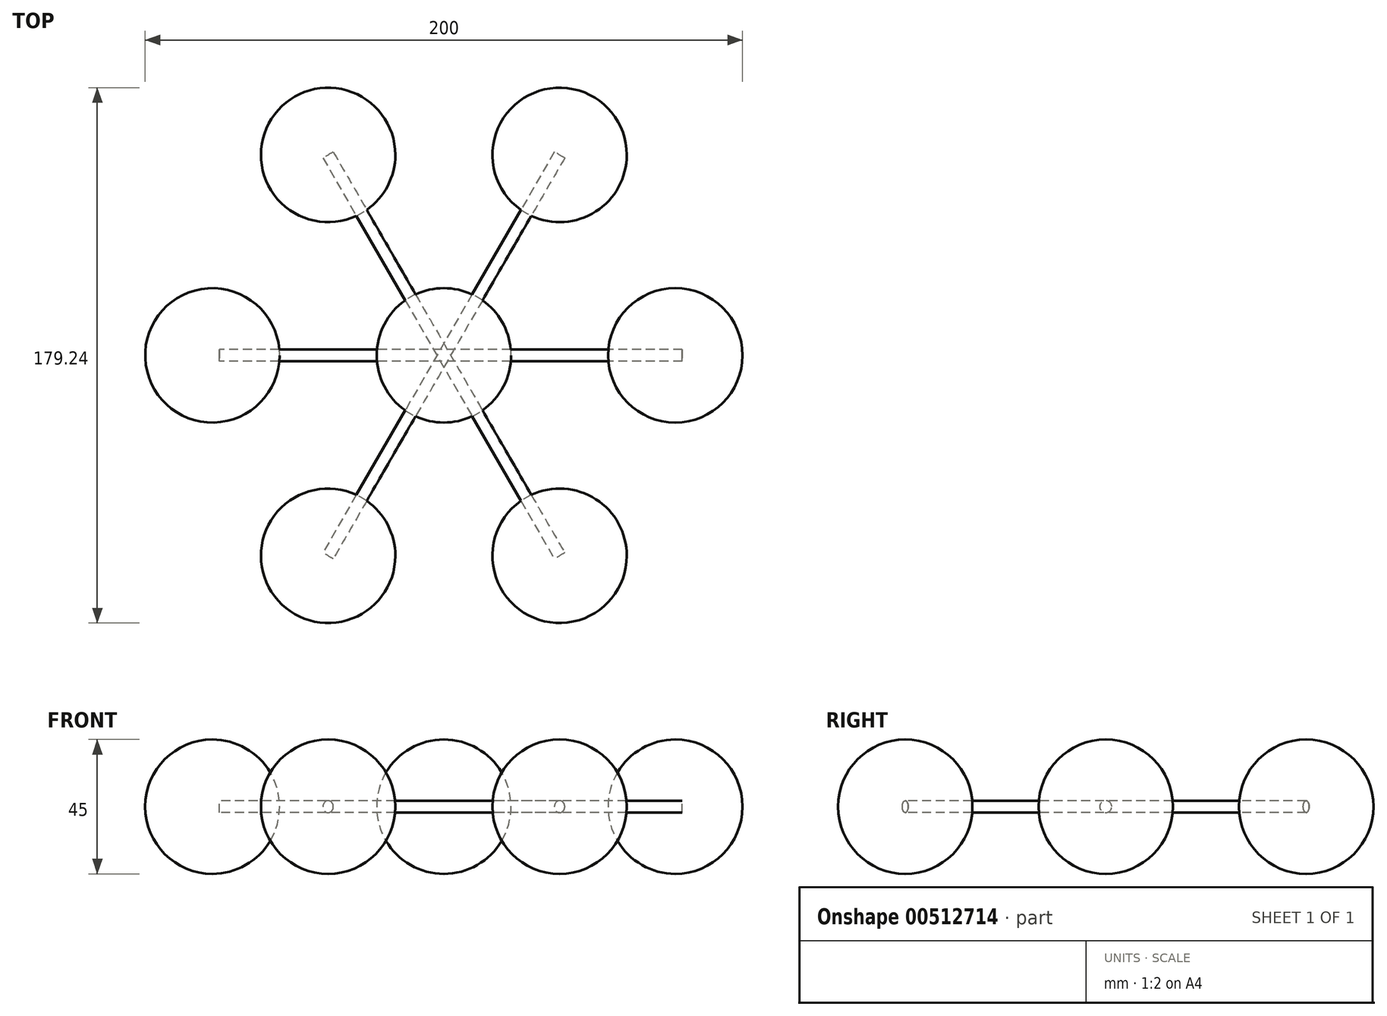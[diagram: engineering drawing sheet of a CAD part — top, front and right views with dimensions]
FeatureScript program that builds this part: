
annotation { "Feature Type Name" : "Feature", "Feature Type Description" : "" }
export const myFeature = defineFeature(function(context is Context, id is Id, definition is map)
    precondition{}
    {
        {
            var Q0;
            Q0=qCreatedBy(makeId("Top.planeOp"),FACE);
            var sketch = newSketch(context, id + "F0", { "sketchPlane" : qUnion([Q0])});
            skPoint(sketch, "E0.center", {"position": v(0, 0) * mm});
            skLineSegment(sketch, "E1", {"start": v(0, 75.54) * mm, "end": v(0, -76.03) * mm, "construction": true});
            skLineSegment(sketch, "E2", {"start": v(-100, 0) * mm, "end": v(100, 0) * mm, "construction": true});
            skLineSegment(sketch, "E3", {"start": v(100, 0) * mm, "end": v(55, 0) * mm});
            skCircle(sketch, "E4", {"center": v(0, 0) * mm, "radius": 22.5 * mm});
            skLineSegment(sketch, "E5", {"start": v(-50, 86.6) * mm, "end": v(0, 0) * mm, "construction": true});
            skLineSegment(sketch, "E6", {"start": v(0, 0) * mm, "end": v(50, 86.6) * mm, "construction": true});
            skLineSegment(sketch, "E7", {"start": v(0, 0) * mm, "end": v(-50, -86.6) * mm, "construction": true});
            skLineSegment(sketch, "E8", {"start": v(0, 0) * mm, "end": v(50, -86.6) * mm, "construction": true});
            skLineSegment(sketch, "E9", {"start": v(50, 86.6) * mm, "end": v(27.5, 47.63) * mm});
            skLineSegment(sketch, "E10", {"start": v(-50, 86.6) * mm, "end": v(-27.5, 47.63) * mm});
            skLineSegment(sketch, "E11", {"start": v(50, -86.6) * mm, "end": v(27.5, -47.63) * mm});
            skLineSegment(sketch, "E12", {"start": v(-50, -86.6) * mm, "end": v(-27.5, -47.63) * mm});
            skCircle(sketch, "E13", {"center": v(-38.75, 67.12) * mm, "radius": 22.5 * mm});
            skCircle(sketch, "E14", {"center": v(38.75, 67.12) * mm, "radius": 22.5 * mm});
            skCircle(sketch, "E15", {"center": v(77.5, 0) * mm, "radius": 22.5 * mm});
            skCircle(sketch, "E16", {"center": v(38.75, -67.12) * mm, "radius": 22.5 * mm});
            skCircle(sketch, "E17", {"center": v(-38.75, -67.12) * mm, "radius": 22.5 * mm});
            skLineSegment(sketch, "E18", {"start": v(-100, 0) * mm, "end": v(-55, 0) * mm});
            skCircle(sketch, "E19", {"center": v(-77.5, 0) * mm, "radius": 22.5 * mm});
            skSolve(sketch);
        }
        {
            var Q0;
            Q0 = qSketchRegion(id + "F0", true);
            extrude(context, id + "F1", {"entities" : qUnion([Q0]), "endBound" : BoundingType.SYMMETRIC, "depth" : 45 * mm});
        }
        {
            var Q0;
            Q0=makeQuery(id+"F1.opExtrude","CAP_FACE",FACE,{"disambiguationData":[OSD([sQuery(id+"F0.wireOp",EDGE,"z0ETdr8p-isuT-aTCR-oVz8-vy0J2JkmRv80")])],"isStart":false});
            var Q1;
            Q1=makeQuery(id+"F1.opExtrude","CAP_FACE",FACE,{"disambiguationData":[OSD([sQuery(id+"F0.wireOp",EDGE,"z0ETdr8p-isuT-aTCR-oVz8-vy0J2JkmRv80")])],"isStart":true});
            var Q2;
            Q2=makeQuery(id+"F1.opExtrude","CAP_FACE",FACE,{"disambiguationData":[OSD([sQuery(id+"F0.wireOp",EDGE,"tVaNseWb-VJnh-5Igu-wT3h-fYb4Q8WA2rvK")])],"isStart":false});
            var Q3;
            Q3=makeQuery(id+"F1.opExtrude","CAP_FACE",FACE,{"disambiguationData":[OSD([sQuery(id+"F0.wireOp",EDGE,"9kzLEHPh-oglC-5A7a-sF2j-jr3aIbh8TAZF")])],"isStart":false});
            var Q4;
            Q4=makeQuery(id+"F1.opExtrude","CAP_FACE",FACE,{"disambiguationData":[OSD([sQuery(id+"F0.wireOp",EDGE,"4IgCiBYZ-ZkFt-cJX4-IA1Z-kr8S1LdGH8R4")])],"isStart":false});
            var Q5;
            Q5=makeQuery(id+"F1.opExtrude","CAP_FACE",FACE,{"disambiguationData":[OSD([sQuery(id+"F0.wireOp",EDGE,"TaNz0faJ-NvhJ-5zIV-Zijx-TU3TPRpmnxcM")])],"isStart":false});
            var Q6;
            Q6=makeQuery(id+"F1.opExtrude","CAP_EDGE",EDGE,{"disambiguationData":[OSD([sQuery(id+"F0.wireOp",EDGE,"tf81Ow77-HOMf-u4hh-1IuM-8iQvc9muZZXg")])],"isStart":false});
            var Q7;
            Q7=makeQuery(id+"F1.opExtrude","CAP_FACE",FACE,{"disambiguationData":[OSD([sQuery(id+"F0.wireOp",EDGE,"tf81Ow77-HOMf-u4hh-1IuM-8iQvc9muZZXg")])],"isStart":true});
            var Q8;
            Q8=makeQuery(id+"F1.opExtrude","CAP_FACE",FACE,{"disambiguationData":[OSD([sQuery(id+"F0.wireOp",EDGE,"TaNz0faJ-NvhJ-5zIV-Zijx-TU3TPRpmnxcM")])],"isStart":true});
            var Q9;
            Q9=makeQuery(id+"F1.opExtrude","CAP_FACE",FACE,{"disambiguationData":[OSD([sQuery(id+"F0.wireOp",EDGE,"4IgCiBYZ-ZkFt-cJX4-IA1Z-kr8S1LdGH8R4")])],"isStart":true});
            var Q10;
            Q10=makeQuery(id+"F1.opExtrude","CAP_FACE",FACE,{"disambiguationData":[OSD([sQuery(id+"F0.wireOp",EDGE,"9kzLEHPh-oglC-5A7a-sF2j-jr3aIbh8TAZF")])],"isStart":true});
            var Q11;
            Q11=makeQuery(id+"F1.opExtrude","CAP_FACE",FACE,{"disambiguationData":[OSD([sQuery(id+"F0.wireOp",EDGE,"tVaNseWb-VJnh-5Igu-wT3h-fYb4Q8WA2rvK")])],"isStart":true});
            var Q12;
            Q12=makeQuery(id+"F1.opExtrude","CAP_FACE",FACE,{"disambiguationData":[OSD([sQuery(id+"F0.wireOp",EDGE,"T7Lpkhv7-mGmL-RBMx-3rt4-JYyUrAoBnvjG")])],"isStart":false});
            var Q13;
            Q13=makeQuery(id+"F1.opExtrude","CAP_FACE",FACE,{"disambiguationData":[OSD([sQuery(id+"F0.wireOp",EDGE,"cKX9D79p-NBMh-DLQl-69uS-r8TYBLCHfCKt")])],"isStart":false});
            var Q14;
            Q14=makeQuery(id+"F1.opExtrude","CAP_FACE",FACE,{"disambiguationData":[OSD([sQuery(id+"F0.wireOp",EDGE,"T7Lpkhv7-mGmL-RBMx-3rt4-JYyUrAoBnvjG")])],"isStart":true});
            var Q15;
            Q15=makeQuery(id+"F1.opExtrude","CAP_FACE",FACE,{"disambiguationData":[OSD([sQuery(id+"F0.wireOp",EDGE,"cKX9D79p-NBMh-DLQl-69uS-r8TYBLCHfCKt")])],"isStart":true});
            var Q16;
            Q16=makeQuery(id+"F1.opExtrude","CAP_FACE",FACE,{"disambiguationData":[OSD([sQuery(id+"F0.wireOp",EDGE,"E4")])],"isStart":false});
            var Q17;
            Q17=makeQuery(id+"F1.opExtrude","CAP_FACE",FACE,{"disambiguationData":[OSD([sQuery(id+"F0.wireOp",EDGE,"E4")])],"isStart":true});
            var Q18;
            Q18=makeQuery(id+"F1.opExtrude","CAP_FACE",FACE,{"disambiguationData":[OSD([sQuery(id+"F0.wireOp",EDGE,"E19")])],"isStart":false});
            var Q19;
            Q19=makeQuery(id+"F1.opExtrude","CAP_FACE",FACE,{"disambiguationData":[OSD([sQuery(id+"F0.wireOp",EDGE,"E13")])],"isStart":false});
            var Q20;
            Q20=makeQuery(id+"F1.opExtrude","CAP_FACE",FACE,{"disambiguationData":[OSD([sQuery(id+"F0.wireOp",EDGE,"E14")])],"isStart":false});
            var Q21;
            Q21=makeQuery(id+"F1.opExtrude","CAP_FACE",FACE,{"disambiguationData":[OSD([sQuery(id+"F0.wireOp",EDGE,"E15")])],"isStart":false});
            var Q22;
            Q22=makeQuery(id+"F1.opExtrude","CAP_FACE",FACE,{"disambiguationData":[OSD([sQuery(id+"F0.wireOp",EDGE,"E16")])],"isStart":false});
            var Q23;
            Q23=makeQuery(id+"F1.opExtrude","CAP_FACE",FACE,{"disambiguationData":[OSD([sQuery(id+"F0.wireOp",EDGE,"E17")])],"isStart":false});
            var Q24;
            Q24=makeQuery(id+"F1.opExtrude","CAP_FACE",FACE,{"disambiguationData":[OSD([sQuery(id+"F0.wireOp",EDGE,"E16")])],"isStart":true});
            var Q25;
            Q25=makeQuery(id+"F1.opExtrude","CAP_FACE",FACE,{"disambiguationData":[OSD([sQuery(id+"F0.wireOp",EDGE,"E17")])],"isStart":true});
            var Q26;
            Q26=makeQuery(id+"F1.opExtrude","CAP_FACE",FACE,{"disambiguationData":[OSD([sQuery(id+"F0.wireOp",EDGE,"E19")])],"isStart":true});
            var Q27;
            Q27=makeQuery(id+"F1.opExtrude","CAP_FACE",FACE,{"disambiguationData":[OSD([sQuery(id+"F0.wireOp",EDGE,"E13")])],"isStart":true});
            var Q28;
            Q28=makeQuery(id+"F1.opExtrude","CAP_FACE",FACE,{"disambiguationData":[OSD([sQuery(id+"F0.wireOp",EDGE,"E15")])],"isStart":true});
            var Q29;
            Q29=makeQuery(id+"F1.opExtrude","CAP_FACE",FACE,{"disambiguationData":[OSD([sQuery(id+"F0.wireOp",EDGE,"E14")])],"isStart":true});
            fillet(context, id + "F2", {"entities" : qUnion([Q0, Q1, Q2, Q3, Q4, Q5, Q6, Q7, Q8, Q9, Q10, Q11, Q12, Q13, Q14, Q15, Q16, Q17, Q18, Q19, Q20, Q21, Q22, Q23, Q24, Q25, Q26, Q27, Q28, Q29]), "radius" : 22.5 * mm, "tangentPropagation" : true, "allowEdgeOverflow" : false});
        }
        {
            var Q0;
            Q0=qCreatedBy(makeId("Right.planeOp"),FACE);
            cPlane(context, id + "F3", {"entities" : qUnion([Q0]), "cplaneType" : CPlaneType.OFFSET, "offset" : 79.8 * mm, "width" : 150 * mm, "height" : 150 * mm});
        }
        {
            var Q0;
            Q0=qCreatedBy(makeId("Top.planeOp"),FACE);
            var sketch = newSketch(context, id + "F4", { "sketchPlane" : qUnion([Q0])});
            skCircle(sketch, "E20", {"center": v(-38.75, 67.12) * mm, "radius": 22.5 * mm});
            skCircle(sketch, "E21", {"center": v(38.75, 67.12) * mm, "radius": 22.5 * mm});
            skCircle(sketch, "E22", {"center": v(77.5, 0) * mm, "radius": 22.5 * mm});
            skCircle(sketch, "E23", {"center": v(38.75, -67.12) * mm, "radius": 22.5 * mm});
            skCircle(sketch, "E24", {"center": v(-38.75, -67.12) * mm, "radius": 22.5 * mm});
            skCircle(sketch, "E25", {"center": v(-77.5, 0) * mm, "radius": 22.5 * mm});
            skCircle(sketch, "E26", {"center": v(0, 0) * mm, "radius": 22.5 * mm});
            skLineSegment(sketch, "E27", {"start": v(-77.5, 0) * mm, "end": v(77.5, 0) * mm});
            skLineSegment(sketch, "E28", {"start": v(-38.75, 67.12) * mm, "end": v(38.75, -67.12) * mm});
            skLineSegment(sketch, "E29", {"start": v(38.75, 67.12) * mm, "end": v(-38.75, -67.12) * mm});
            skSolve(sketch);
        }
        {
            var Q0;
            Q0=qCreatedBy(id+"F3.planeOp",FACE);
            var sketch = newSketch(context, id + "F5", { "sketchPlane" : qUnion([Q0])});
            skCircle(sketch, "E30", {"center": v(0, 0) * mm, "radius": 2 * mm});
            skSolve(sketch);
        }
        {
            var Q0;
            Q0 = qSketchRegion(id + "F5", true);
            var Q1;
            Q1=sQuery(id+"F4.wireOp",EDGE,"E27");
            sweep(context, id + "F6", {"profiles" : qUnion([Q0]), "path" : qUnion([Q1])});
        }
        {
            var Q0;
            Q0=sQuery(id+"F4.wireOp",VERTEX,"E20.center");
            var Q1;
            Q1=sQuery(id+"F4.wireOp",EDGE,"E28");
            cPlane(context, id + "F7", {"entities" : qUnion([Q0, Q1]), "cplaneType" : CPlaneType.LINE_POINT, "offset" : 25 * mm, "width" : 150 * mm, "height" : 150 * mm});
        }
        {
            var Q0;
            Q0=qCreatedBy(id+"F7.planeOp",FACE);
            var sketch = newSketch(context, id + "F8", { "sketchPlane" : qUnion([Q0])});
            skCircle(sketch, "E31", {"center": v(0, 0) * mm, "radius": 2 * mm});
            skSolve(sketch);
        }
        {
            var Q0;
            Q0 = qSketchRegion(id + "F8", true);
            var Q1;
            Q1=sQuery(id+"F4.wireOp",EDGE,"E28");
            sweep(context, id + "F9", {"profiles" : qUnion([Q0]), "path" : qUnion([Q1])});
        }
        {
            var Q0;
            Q0=sQuery(id+"F4.wireOp",EDGE,"E29");
            var Q1;
            Q1=sQuery(id+"F4.wireOp",VERTEX,"E21.center");
            cPlane(context, id + "F10", {"entities" : qUnion([Q0, Q1]), "cplaneType" : CPlaneType.LINE_POINT, "offset" : 25 * mm, "width" : 150 * mm, "height" : 150 * mm});
        }
        {
            var Q0;
            Q0=qCreatedBy(id+"F10.planeOp",FACE);
            var sketch = newSketch(context, id + "F11", { "sketchPlane" : qUnion([Q0])});
            skCircle(sketch, "E32", {"center": v(0, 0) * mm, "radius": 2 * mm});
            skSolve(sketch);
        }
        {
            var Q0;
            Q0 = qSketchRegion(id + "F11", true);
            var Q1;
            Q1=sQuery(id+"F4.wireOp",EDGE,"E29");
            sweep(context, id + "F12", {"profiles" : qUnion([Q0]), "path" : qUnion([Q1])});
        }
    });
